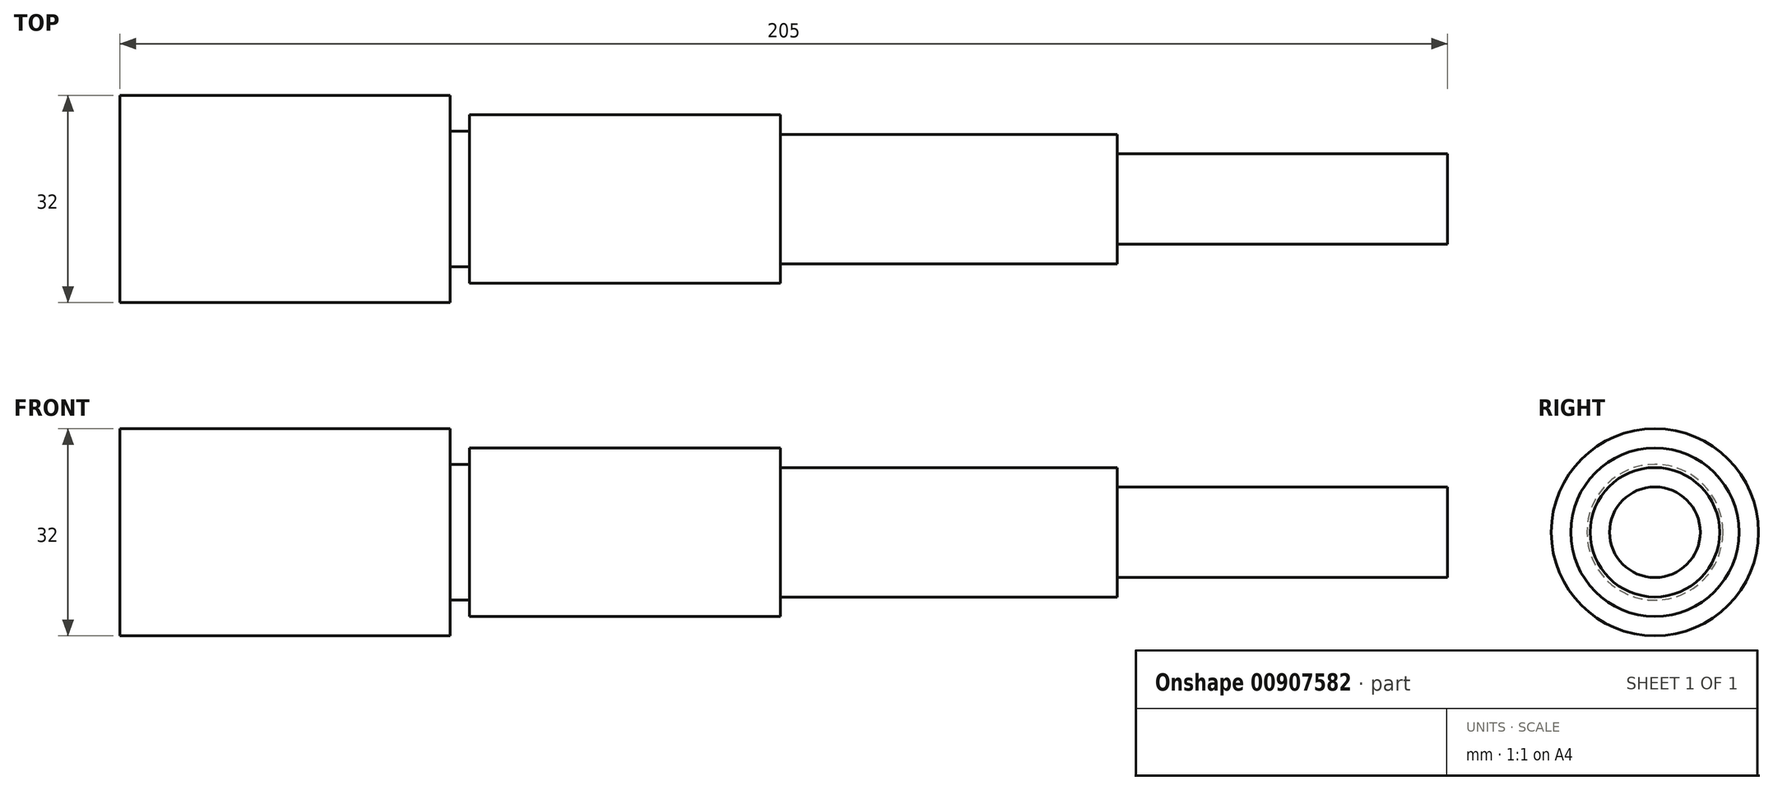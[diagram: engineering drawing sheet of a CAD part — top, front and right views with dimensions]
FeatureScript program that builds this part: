
annotation { "Feature Type Name" : "Feature", "Feature Type Description" : "" }
export const myFeature = defineFeature(function(context is Context, id is Id, definition is map)
    precondition{}
    {
        {
            var Q0;
            Q0=qCreatedBy(makeId("Front.planeOp"),FACE);
            var sketch = newSketch(context, id + "F0", { "sketchPlane" : qUnion([Q0])});
            skLineSegment(sketch, "E0", {"start": v(0, 0) * mm, "end": v(-205, 0) * mm});
            skLineSegment(sketch, "E1", {"start": v(-205, 0) * mm, "end": v(-205, 16) * mm});
            skLineSegment(sketch, "E2", {"start": v(-205, 16) * mm, "end": v(-154, 16) * mm});
            skLineSegment(sketch, "E3", {"start": v(-154, 16) * mm, "end": v(-154, 13) * mm});
            skLineSegment(sketch, "E4", {"start": v(-151, 13) * mm, "end": v(-103, 13) * mm});
            skLineSegment(sketch, "E5", {"start": v(-103, 13) * mm, "end": v(-103, 10) * mm});
            skLineSegment(sketch, "E6", {"start": v(-103, 10) * mm, "end": v(-51, 10) * mm});
            skLineSegment(sketch, "E7", {"start": v(-51, 10) * mm, "end": v(-51, 7) * mm});
            skLineSegment(sketch, "E8", {"start": v(-51, 7) * mm, "end": v(0, 7) * mm});
            skLineSegment(sketch, "E9", {"start": v(0, 7) * mm, "end": v(0, 0) * mm});
            skLineSegment(sketch, "E10", {"start": v(-154, 13) * mm, "end": v(-154, 10.5) * mm});
            skLineSegment(sketch, "E11", {"start": v(-154, 10.5) * mm, "end": v(-151, 10.5) * mm});
            skLineSegment(sketch, "E12", {"start": v(-151, 10.5) * mm, "end": v(-151, 13) * mm});
            skSolve(sketch);
        }
        {
            var Q0;
            Q0=makeQuery(id+"F0.imprint","IMPRINT",FACE,{"disambiguationData":[TD([[makeQuery(id+"F0.imprint","IMPRINT",EDGE,{"derivedFrom":sQuery(id+"F0.wireOp",EDGE,"E0")}),-1.0]])]});
            var Q1;
            Q1=sQuery(id+"F0.wireOp",EDGE,"E0");
            revolve(context, id + "F1", {"surfaceOperationType" : NewSurfaceOperationType.NEW, "entities" : qUnion([Q0]), "axis" : qUnion([Q1]), "revolveType" : RevolveType.FULL});
        }
    });
